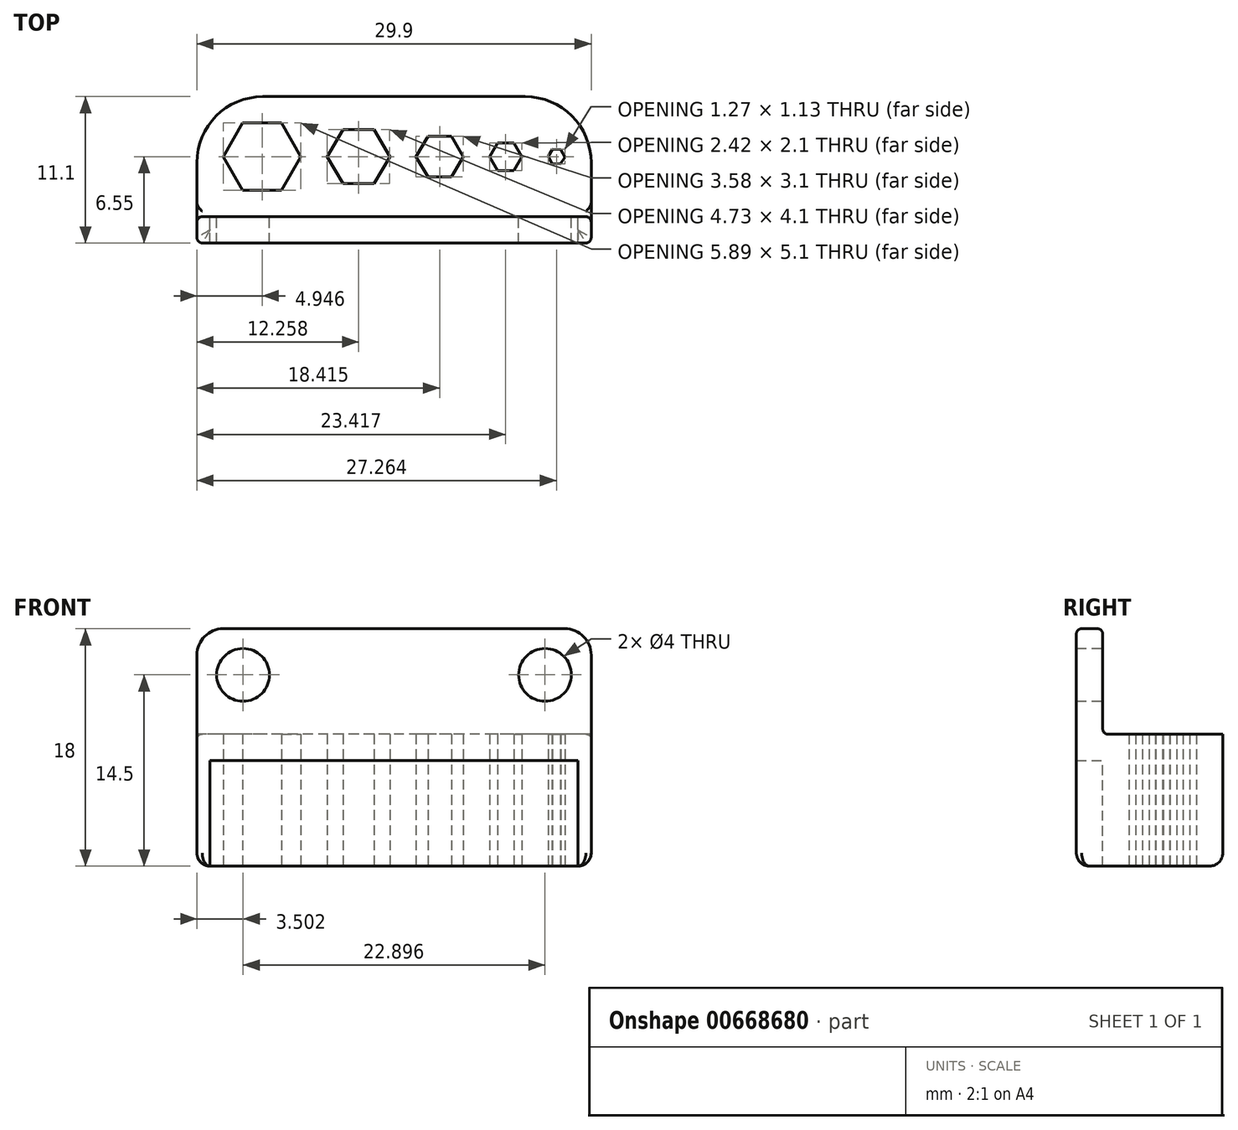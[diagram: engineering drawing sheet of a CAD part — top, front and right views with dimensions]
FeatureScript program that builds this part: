
annotation { "Feature Type Name" : "Feature", "Feature Type Description" : "" }
export const myFeature = defineFeature(function(context is Context, id is Id, definition is map)
    precondition{}
    {
        {
            var Q0;
            Q0=qCreatedBy(makeId("Top.planeOp"),FACE);
            var sketch = newSketch(context, id + "F0", { "sketchPlane" : qUnion([Q0])});
            skLineSegment(sketch, "E0.bottom", {"start": v(14.95, 4.55) * mm, "end": v(-14.95, 4.55) * mm});
            skLineSegment(sketch, "E0.top", {"start": v(14.95, -4.55) * mm, "end": v(-14.95, -4.55) * mm});
            skLineSegment(sketch, "E0.left", {"start": v(14.95, 4.55) * mm, "end": v(14.95, -4.55) * mm});
            skLineSegment(sketch, "E0.right", {"start": v(-14.95, 4.55) * mm, "end": v(-14.95, -4.55) * mm});
            skPoint(sketch, "E0.middle", {"position": v(0, 0) * mm});
            skLineSegment(sketch, "E1", {"start": v(-14.95, 0) * mm, "end": v(14.95, 0) * mm, "construction": true});
            skCircle(sketch, "E2.cCircle", {"center": v(-10, 0) * mm, "radius": 2.55 * mm, "construction": true});
            skLineSegment(sketch, "E2.0", {"start": v(-7.06, 0) * mm, "end": v(-8.53, -2.55) * mm});
            skLineSegment(sketch, "E2.1", {"start": v(-8.53, -2.55) * mm, "end": v(-11.48, -2.55) * mm});
            skLineSegment(sketch, "E2.2", {"start": v(-11.48, -2.55) * mm, "end": v(-12.95, 0) * mm});
            skLineSegment(sketch, "E2.3", {"start": v(-12.95, 0) * mm, "end": v(-11.48, 2.55) * mm});
            skLineSegment(sketch, "E2.4", {"start": v(-11.48, 2.55) * mm, "end": v(-8.53, 2.55) * mm});
            skLineSegment(sketch, "E2.5", {"start": v(-8.53, 2.55) * mm, "end": v(-7.06, 0) * mm});
            skPoint(sketch, "E2.0.midPoint", {"position": v(-7.8, -1.27) * mm});
            skCircle(sketch, "E3.cCircle", {"center": v(-2.7, 0) * mm, "radius": 2.05 * mm, "construction": true});
            skLineSegment(sketch, "E3.0", {"start": v(-1.5, -2.05) * mm, "end": v(-3.88, -2.05) * mm});
            skLineSegment(sketch, "E3.1", {"start": v(-3.88, -2.05) * mm, "end": v(-5.06, 0) * mm});
            skLineSegment(sketch, "E3.2", {"start": v(-5.06, 0) * mm, "end": v(-3.88, 2.05) * mm});
            skLineSegment(sketch, "E3.3", {"start": v(-3.88, 2.05) * mm, "end": v(-1.5, 2.05) * mm});
            skLineSegment(sketch, "E3.4", {"start": v(-1.5, 2.05) * mm, "end": v(-0.32, 0) * mm});
            skLineSegment(sketch, "E3.5", {"start": v(-0.32, 0) * mm, "end": v(-1.5, -2.05) * mm});
            skPoint(sketch, "E3.0.midPoint", {"position": v(-2.7, -2.05) * mm});
            skCircle(sketch, "E4.cCircle", {"center": v(3.46, 0) * mm, "radius": 1.55 * mm, "construction": true});
            skLineSegment(sketch, "E4.0", {"start": v(4.36, -1.55) * mm, "end": v(2.57, -1.55) * mm});
            skLineSegment(sketch, "E4.1", {"start": v(2.57, -1.55) * mm, "end": v(1.68, 0) * mm});
            skLineSegment(sketch, "E4.2", {"start": v(1.68, 0) * mm, "end": v(2.57, 1.55) * mm});
            skLineSegment(sketch, "E4.3", {"start": v(2.57, 1.55) * mm, "end": v(4.36, 1.55) * mm});
            skLineSegment(sketch, "E4.4", {"start": v(4.36, 1.55) * mm, "end": v(5.25, 0) * mm});
            skLineSegment(sketch, "E4.5", {"start": v(5.25, 0) * mm, "end": v(4.36, -1.55) * mm});
            skPoint(sketch, "E4.0.midPoint", {"position": v(3.46, -1.55) * mm});
            skCircle(sketch, "E5.cCircle", {"center": v(8.47, 0) * mm, "radius": 1.05 * mm, "construction": true});
            skLineSegment(sketch, "E5.0", {"start": v(9.68, 0) * mm, "end": v(9.07, -1.05) * mm});
            skLineSegment(sketch, "E5.1", {"start": v(9.07, -1.05) * mm, "end": v(7.86, -1.05) * mm});
            skLineSegment(sketch, "E5.2", {"start": v(7.86, -1.05) * mm, "end": v(7.25, 0) * mm});
            skLineSegment(sketch, "E5.3", {"start": v(7.25, 0) * mm, "end": v(7.86, 1.05) * mm});
            skLineSegment(sketch, "E5.4", {"start": v(7.86, 1.05) * mm, "end": v(9.07, 1.05) * mm});
            skLineSegment(sketch, "E5.5", {"start": v(9.07, 1.05) * mm, "end": v(9.68, 0) * mm});
            skPoint(sketch, "E5.0.midPoint", {"position": v(9.38, -0.53) * mm});
            skCircle(sketch, "E6.cCircle", {"center": v(12.31, 0) * mm, "radius": 0.55 * mm, "construction": true});
            skLineSegment(sketch, "E6.0", {"start": v(11.68, 0.03) * mm, "end": v(12.02, 0.57) * mm});
            skLineSegment(sketch, "E6.1", {"start": v(12.02, 0.57) * mm, "end": v(12.66, 0.53) * mm});
            skLineSegment(sketch, "E6.2", {"start": v(12.66, 0.53) * mm, "end": v(12.95, -0.03) * mm});
            skLineSegment(sketch, "E6.3", {"start": v(12.95, -0.03) * mm, "end": v(12.6, -0.57) * mm});
            skLineSegment(sketch, "E6.4", {"start": v(12.6, -0.57) * mm, "end": v(11.97, -0.53) * mm});
            skLineSegment(sketch, "E6.5", {"start": v(11.97, -0.53) * mm, "end": v(11.68, 0.03) * mm});
            skPoint(sketch, "E6.0.midPoint", {"position": v(11.85, 0.3) * mm});
            skSolve(sketch);
        }
        {
            var Q0;
            Q0=makeQuery(id+"F0.imprint","IMPRINT",FACE,{"disambiguationData":[TD([[makeQuery(id+"F0.imprint","IMPRINT",EDGE,{"derivedFrom":sQuery(id+"F0.wireOp",EDGE,"E0.bottom")}),1.0]])]});
            extrude(context, id + "F1", {"entities" : qUnion([Q0]), "depth" : 10 * mm, "offsetDistance" : 25 * mm});
        }
        {
            var Q0;
            Q0=makeQuery(id+"F1.opExtrude","SWEPT_FACE",FACE,{"disambiguationData":[OSD([sQuery(id+"F0.wireOp",EDGE,"E0.top")])]});
            var sketch = newSketch(context, id + "F2", { "sketchPlane" : qUnion([Q0])});
            skLineSegment(sketch, "E7", {"start": v(-14.95, 10) * mm, "end": v(-14.95, 16) * mm});
            skLineSegment(sketch, "E8", {"start": v(-12.95, 18) * mm, "end": v(12.95, 18) * mm});
            skLineSegment(sketch, "E9", {"start": v(14.95, 16) * mm, "end": v(14.95, 10) * mm});
            skLineSegment(sketch, "E10", {"start": v(14.95, 10) * mm, "end": v(14.95, 0) * mm});
            skLineSegment(sketch, "E11", {"start": v(14.95, 0) * mm, "end": v(13.95, 0) * mm});
            skLineSegment(sketch, "E12", {"start": v(13.95, 0) * mm, "end": v(13.95, 8) * mm});
            skLineSegment(sketch, "E13", {"start": v(13.95, 8) * mm, "end": v(-13.95, 8) * mm});
            skLineSegment(sketch, "E14", {"start": v(-13.95, 8) * mm, "end": v(-13.95, 0) * mm});
            skLineSegment(sketch, "E15", {"start": v(-13.95, 0) * mm, "end": v(-14.95, 0) * mm});
            skLineSegment(sketch, "E16", {"start": v(-14.95, 0) * mm, "end": v(-14.95, 10) * mm});
            skCircle(sketch, "E17", {"center": v(-11.45, 14.5) * mm, "radius": 2 * mm});
            skCircle(sketch, "E18", {"center": v(11.45, 14.5) * mm, "radius": 2 * mm});
            skPoint(sketch, "E19.visualSharp", {"position": v(-14.95, 18) * mm});
            skArc(sketch, "E19.filletArc", {"start": v(-12.95, 18) * mm, "mid": v(-14.36, 17.41) * mm, "end": v(-14.95, 16) * mm});
            skPoint(sketch, "E20.visualSharp", {"position": v(14.95, 18) * mm});
            skArc(sketch, "E20.filletArc", {"start": v(14.95, 16) * mm, "mid": v(14.36, 17.41) * mm, "end": v(12.95, 18) * mm});
            skSolve(sketch);
        }
        {
            var Q0;
            Q0 = qSketchRegion(id + "F2", true);
            extrude(context, id + "F3", {"entities" : qUnion([Q0]), "operationType" : NewBodyOperationType.ADD, "depth" : 2 * mm, "offsetDistance" : 25 * mm});
        }
        {
            var Q0;
            Q0=makeQuery(id+"F1.opExtrude","SWEPT_EDGE",EDGE,{"disambiguationData":[OSD([sQuery(id+"F0.wireOp",EDGE,"E0.bottom"),sQuery(id+"F0.wireOp",EDGE,"E0.left")])]});
            var Q1;
            Q1=makeQuery(id+"F1.opExtrude","SWEPT_EDGE",EDGE,{"disambiguationData":[OSD([sQuery(id+"F0.wireOp",EDGE,"E0.bottom"),sQuery(id+"F0.wireOp",EDGE,"E0.right")])]});
            fillet(context, id + "F4", {"entities" : qUnion([Q0, Q1]), "radius" : 5 * mm, "tangentPropagation" : true, "allowEdgeOverflow" : false});
        }
        {
            var Q0;
            Q0=makeQuery(id+"F1.opExtrude","CAP_EDGE",EDGE,{"disambiguationData":[OSD([sQuery(id+"F0.wireOp",EDGE,"E0.top")])],"isStart":false});
            var Q1;
            Q1=makeQuery(id+"F3.opExtrude","CAP_EDGE",EDGE,{"disambiguationData":[OSD([sQuery(id+"F2.wireOp",EDGE,"E9"),sQuery(id+"F2.wireOp",EDGE,"E10")])],"isStart":false});
            var Q2;
            Q2=makeQuery(id+"F3.opExtrude","CAP_EDGE",EDGE,{"disambiguationData":[OSD([sQuery(id+"F2.wireOp",EDGE,"E8")])],"isStart":true});
            fillet(context, id + "F5", {"entities" : qUnion([Q0, Q1, Q2]), "radius" : 0.4 * mm, "tangentPropagation" : true, "allowEdgeOverflow" : false});
        }
        {
            var Q0;
            Q0=makeQuery(id+"F3.boolean.opBoolean","MERGE",EDGE,{"derivedFrom":[makeQuery(id+"F1.opExtrude","CAP_EDGE",EDGE,{"disambiguationData":[OSD([sQuery(id+"F0.wireOp",EDGE,"E0.right")])],"isStart":true}),makeQuery(id+"F3.opExtrude","SWEPT_EDGE",EDGE,{"disambiguationData":[OSD([sQuery(id+"F2.wireOp",EDGE,"E15"),sQuery(id+"F2.wireOp",EDGE,"E16")])]})]});
            fillet(context, id + "F6", {"entities" : qUnion([Q0]), "radius" : 1 * mm, "tangentPropagation" : true, "allowEdgeOverflow" : false});
        }
    });
